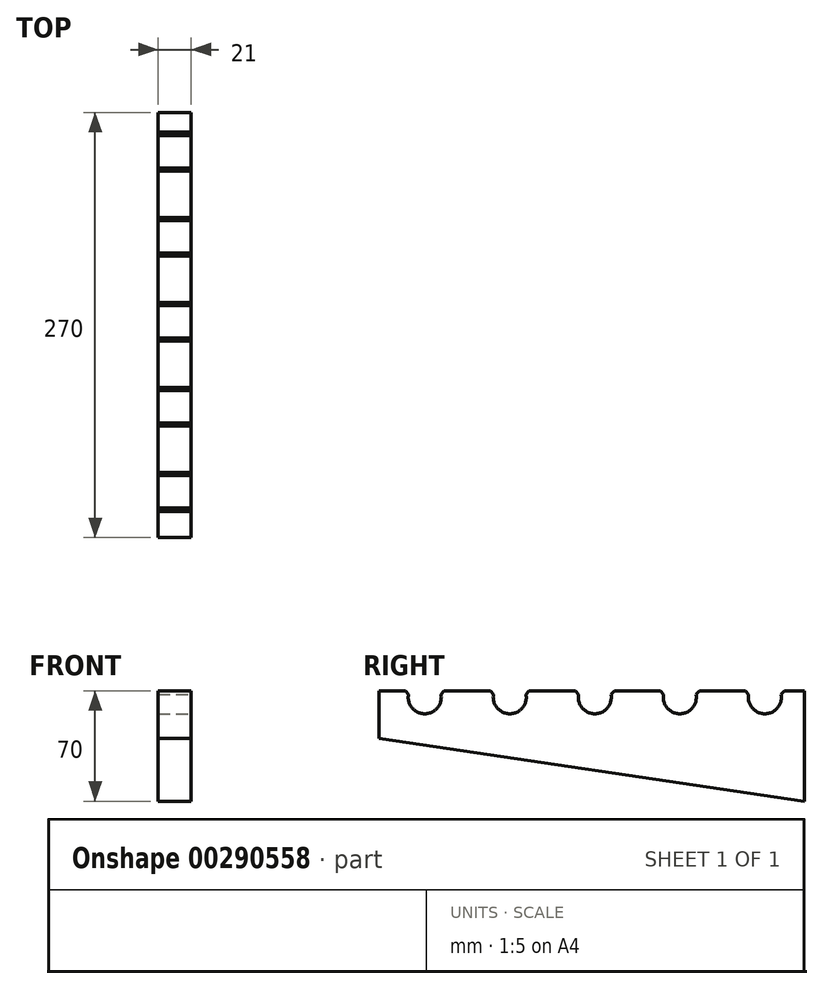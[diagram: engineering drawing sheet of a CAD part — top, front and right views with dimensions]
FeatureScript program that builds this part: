
annotation { "Feature Type Name" : "Feature", "Feature Type Description" : "" }
export const myFeature = defineFeature(function(context is Context, id is Id, definition is map)
    precondition{}
    {
        {
            var Q0;
            Q0=qCreatedBy(makeId("Right.planeOp"),FACE);
            var sketch = newSketch(context, id + "F0", { "sketchPlane" : qUnion([Q0])});
            skLineSegment(sketch, "E0", {"start": v(135, -45) * mm, "end": v(-135, -5) * mm});
            skLineSegment(sketch, "E1", {"start": v(-135, -5) * mm, "end": v(-135, 25) * mm});
            skLineSegment(sketch, "E2", {"start": v(-135, 25) * mm, "end": v(135, 25) * mm});
            skLineSegment(sketch, "E3", {"start": v(135, 25) * mm, "end": v(135, -45) * mm});
            skSolve(sketch);
        }
        {
            var Q0;
            Q0 = qSketchRegion(id + "F0", true);
            extrude(context, id + "F1", {"entities" : qUnion([Q0]), "depth" : 21 * mm});
        }
        {
            var Q0;
            Q0=makeQuery(id+"F1.opExtrude","CAP_FACE",FACE,{"disambiguationData":[OSD([sQuery(id+"F0.wireOp",EDGE,"E0"),sQuery(id+"F0.wireOp",EDGE,"E1"),sQuery(id+"F0.wireOp",EDGE,"E2"),sQuery(id+"F0.wireOp",EDGE,"E3")])],"isStart":false});
            var sketch = newSketch(context, id + "F2", { "sketchPlane" : qUnion([Q0])});
            skLineSegment(sketch, "E4", {"start": v(155.2, 21) * mm, "end": v(-167.63, 21) * mm, "construction": true});
            skCircle(sketch, "E5", {"center": v(110, 21) * mm, "radius": 10.5 * mm});
            skCircle(sketch, "E6.1.0.0", {"center": v(56, 21) * mm, "radius": 10.5 * mm});
            skLineSegment(sketch, "E6.1.0.1", {"start": v(101.2, 21) * mm, "end": v(-221.63, 21) * mm, "construction": true});
            skCircle(sketch, "E6.2.0.0", {"center": v(2, 21) * mm, "radius": 10.5 * mm});
            skLineSegment(sketch, "E6.2.0.1", {"start": v(47.2, 21) * mm, "end": v(-275.63, 21) * mm, "construction": true});
            skCircle(sketch, "E6.3.0.0", {"center": v(-52, 21) * mm, "radius": 10.5 * mm});
            skLineSegment(sketch, "E6.3.0.1", {"start": v(-6.8, 21) * mm, "end": v(-329.63, 21) * mm, "construction": true});
            skCircle(sketch, "E6.4.0.0", {"center": v(-106, 21) * mm, "radius": 10.5 * mm});
            skLineSegment(sketch, "E6.4.0.1", {"start": v(-60.8, 21) * mm, "end": v(-383.63, 21) * mm, "construction": true});
            skLineSegment(sketch, "E6.direction1", {"start": v(110, 21) * mm, "end": v(56, 21) * mm, "construction": true});
            skSolve(sketch);
        }
        {
            var Q0;
            Q0 = qSketchRegion(id + "F2", true);
            extrude(context, id + "F3", {"entities" : qUnion([Q0]), "operationType" : NewBodyOperationType.REMOVE, "oppositeDirection" : true, "depth" : 25 * mm});
        }
        {
            var Q0;
            Q0=makeQuery(id+"F3.boolean.opBoolean","INTERSECT",EDGE,{"disambiguationData":[OD(1.0)],"derivedFrom":[makeQuery(id+"F1.opExtrude","SWEPT_FACE",FACE,{"disambiguationData":[OSD([sQuery(id+"F0.wireOp",EDGE,"E2")])]}),makeQuery(id+"F3.opExtrude","SWEPT_FACE",FACE,{"disambiguationData":[OSD([sQuery(id+"F2.wireOp",EDGE,"E6.4.0.0")])]})]});
            var Q1;
            Q1=makeQuery(id+"F3.boolean.opBoolean","INTERSECT",EDGE,{"disambiguationData":[OD(0.0)],"derivedFrom":[makeQuery(id+"F1.opExtrude","SWEPT_FACE",FACE,{"disambiguationData":[OSD([sQuery(id+"F0.wireOp",EDGE,"E2")])]}),makeQuery(id+"F3.opExtrude","SWEPT_FACE",FACE,{"disambiguationData":[OSD([sQuery(id+"F2.wireOp",EDGE,"E6.4.0.0")])]})]});
            var Q2;
            Q2=makeQuery(id+"F3.boolean.opBoolean","INTERSECT",EDGE,{"disambiguationData":[OD(1.0)],"derivedFrom":[makeQuery(id+"F1.opExtrude","SWEPT_FACE",FACE,{"disambiguationData":[OSD([sQuery(id+"F0.wireOp",EDGE,"E2")])]}),makeQuery(id+"F3.opExtrude","SWEPT_FACE",FACE,{"disambiguationData":[OSD([sQuery(id+"F2.wireOp",EDGE,"E6.3.0.0")])]})]});
            var Q3;
            Q3=makeQuery(id+"F3.boolean.opBoolean","INTERSECT",EDGE,{"disambiguationData":[OD(0.0)],"derivedFrom":[makeQuery(id+"F1.opExtrude","SWEPT_FACE",FACE,{"disambiguationData":[OSD([sQuery(id+"F0.wireOp",EDGE,"E2")])]}),makeQuery(id+"F3.opExtrude","SWEPT_FACE",FACE,{"disambiguationData":[OSD([sQuery(id+"F2.wireOp",EDGE,"E6.3.0.0")])]})]});
            var Q4;
            Q4=makeQuery(id+"F3.boolean.opBoolean","INTERSECT",EDGE,{"disambiguationData":[OD(1.0)],"derivedFrom":[makeQuery(id+"F1.opExtrude","SWEPT_FACE",FACE,{"disambiguationData":[OSD([sQuery(id+"F0.wireOp",EDGE,"E2")])]}),makeQuery(id+"F3.opExtrude","SWEPT_FACE",FACE,{"disambiguationData":[OSD([sQuery(id+"F2.wireOp",EDGE,"E6.2.0.0")])]})]});
            var Q5;
            Q5=makeQuery(id+"F3.boolean.opBoolean","INTERSECT",EDGE,{"disambiguationData":[OD(0.0)],"derivedFrom":[makeQuery(id+"F1.opExtrude","SWEPT_FACE",FACE,{"disambiguationData":[OSD([sQuery(id+"F0.wireOp",EDGE,"E2")])]}),makeQuery(id+"F3.opExtrude","SWEPT_FACE",FACE,{"disambiguationData":[OSD([sQuery(id+"F2.wireOp",EDGE,"E6.2.0.0")])]})]});
            var Q6;
            Q6=makeQuery(id+"F3.boolean.opBoolean","INTERSECT",EDGE,{"disambiguationData":[OD(1.0)],"derivedFrom":[makeQuery(id+"F1.opExtrude","SWEPT_FACE",FACE,{"disambiguationData":[OSD([sQuery(id+"F0.wireOp",EDGE,"E2")])]}),makeQuery(id+"F3.opExtrude","SWEPT_FACE",FACE,{"disambiguationData":[OSD([sQuery(id+"F2.wireOp",EDGE,"E6.1.0.0")])]})]});
            var Q7;
            Q7=makeQuery(id+"F3.boolean.opBoolean","INTERSECT",EDGE,{"disambiguationData":[OD(0.0)],"derivedFrom":[makeQuery(id+"F1.opExtrude","SWEPT_FACE",FACE,{"disambiguationData":[OSD([sQuery(id+"F0.wireOp",EDGE,"E2")])]}),makeQuery(id+"F3.opExtrude","SWEPT_FACE",FACE,{"disambiguationData":[OSD([sQuery(id+"F2.wireOp",EDGE,"E6.1.0.0")])]})]});
            var Q8;
            Q8=makeQuery(id+"F3.boolean.opBoolean","INTERSECT",EDGE,{"disambiguationData":[OD(1.0)],"derivedFrom":[makeQuery(id+"F1.opExtrude","SWEPT_FACE",FACE,{"disambiguationData":[OSD([sQuery(id+"F0.wireOp",EDGE,"E2")])]}),makeQuery(id+"F3.opExtrude","SWEPT_FACE",FACE,{"disambiguationData":[OSD([sQuery(id+"F2.wireOp",EDGE,"E5")])]})]});
            var Q9;
            Q9=makeQuery(id+"F3.boolean.opBoolean","INTERSECT",EDGE,{"disambiguationData":[OD(0.0)],"derivedFrom":[makeQuery(id+"F1.opExtrude","SWEPT_FACE",FACE,{"disambiguationData":[OSD([sQuery(id+"F0.wireOp",EDGE,"E2")])]}),makeQuery(id+"F3.opExtrude","SWEPT_FACE",FACE,{"disambiguationData":[OSD([sQuery(id+"F2.wireOp",EDGE,"E5")])]})]});
            chamfer(context, id + "F4", {"entities" : qUnion([Q0, Q1, Q2, Q3, Q4, Q5, Q6, Q7, Q8, Q9]), "width" : 2 * mm, "tangentPropagation" : true});
        }
    });
